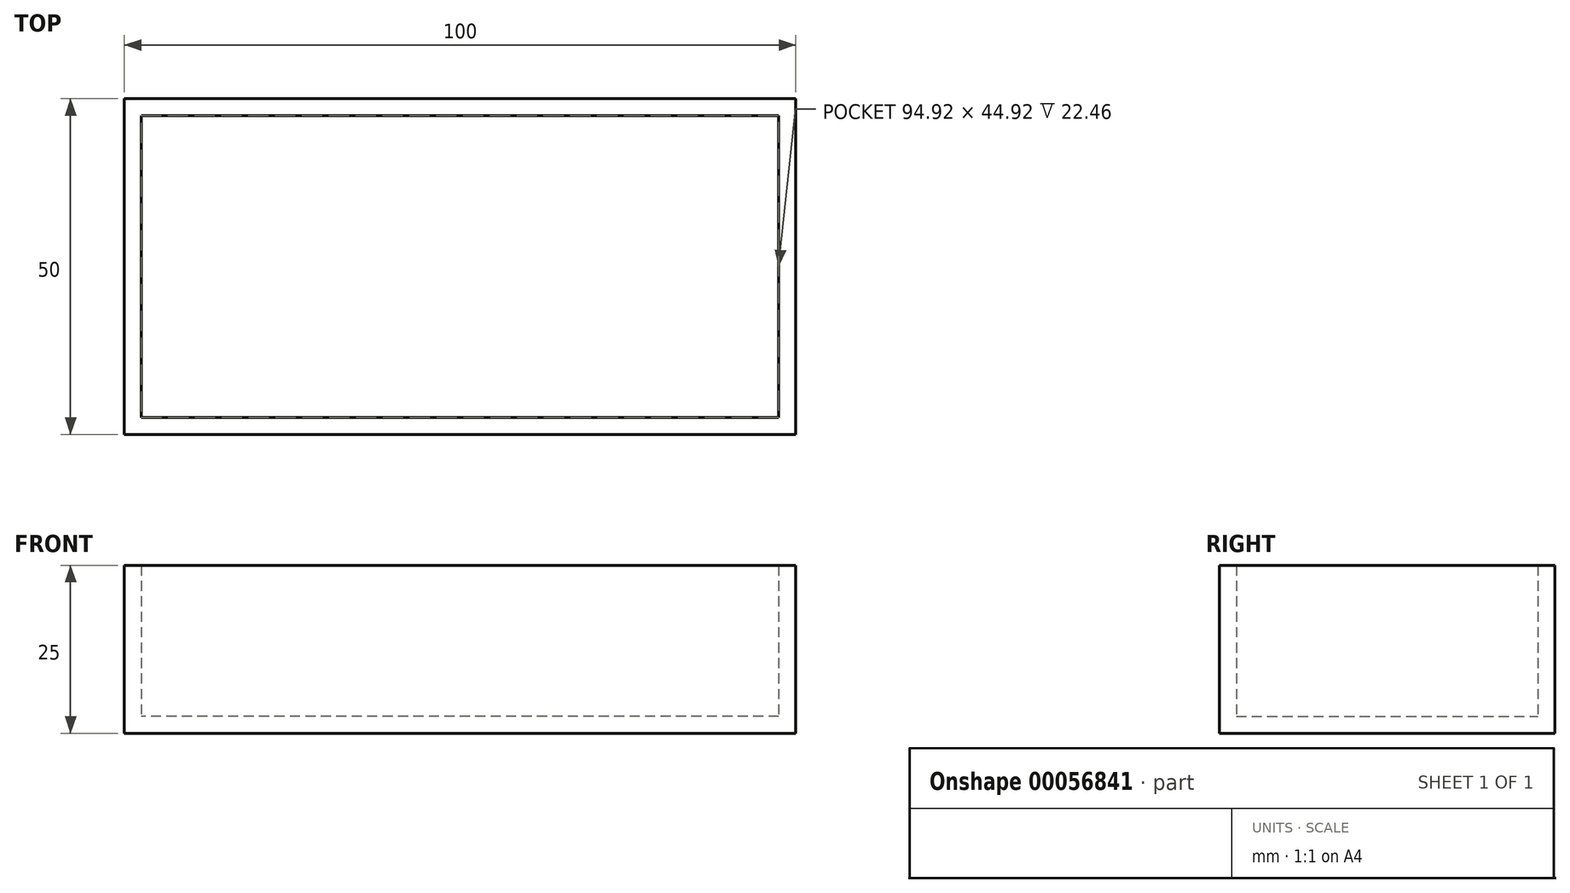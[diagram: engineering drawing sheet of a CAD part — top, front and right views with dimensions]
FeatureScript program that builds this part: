
annotation { "Feature Type Name" : "Feature", "Feature Type Description" : "" }
export const myFeature = defineFeature(function(context is Context, id is Id, definition is map)
    precondition{}
    {
        {
            var Q0;
            Q0=qCreatedBy(makeId("Top.planeOp"),FACE);
            var sketch = newSketch(context, id + "F0", { "sketchPlane" : qUnion([Q0])});
            skLineSegment(sketch, "E0.rect.bottom", {"start": v(50, -25) * mm, "end": v(-50, -25) * mm});
            skLineSegment(sketch, "E0.rect.top", {"start": v(50, 25) * mm, "end": v(-50, 25) * mm});
            skLineSegment(sketch, "E0.rect.left", {"start": v(50, -25) * mm, "end": v(50, 25) * mm});
            skLineSegment(sketch, "E0.rect.right", {"start": v(-50, -25) * mm, "end": v(-50, 25) * mm});
            skPoint(sketch, "E0.rect.middle", {"position": v(0, 0) * mm});
            skSolve(sketch);
        }
        {
            var Q0;
            Q0 = qSketchRegion(id + "F0", true);
            extrude(context, id + "F1", {"entities" : qUnion([Q0]), "depth" : 25 * mm});
        }
        {
            var Q0;
            Q0=makeQuery(id+"F1.opExtrude","CAP_FACE",FACE,{"disambiguationData":[OSD([sQuery(id+"F0.wireOp",EDGE,"E0.rect.bottom"),sQuery(id+"F0.wireOp",EDGE,"E0.rect.top"),sQuery(id+"F0.wireOp",EDGE,"E0.rect.left"),sQuery(id+"F0.wireOp",EDGE,"E0.rect.right")])],"isStart":false});
            shell(context, id + "F2", {"entities" : qUnion([Q0]), "thickness" : 2.54 * mm});
        }
        {
            var Q0;
            Q0=makeQuery(id+"F1.opExtrude","SWEPT_FACE",FACE,{"disambiguationData":[OSD([sQuery(id+"F0.wireOp",EDGE,"E0.rect.left")])]});
            var sketch = newSketch(context, id + "F3", { "sketchPlane" : qUnion([Q0])});
            skCircle(sketch, "E1", {"center": v(0, 13.07) * mm, "radius": 7.87 * mm});
            skSolve(sketch);
        }
        {
            var Q0;
            Q0 = qSketchRegion(id + "F3", true);
            extrude(context, id + "F4", {"entities" : qUnion([Q0]), "operationType" : NewBodyOperationType.REMOVE, "depth" : 25.4 * mm});
        }
    });
